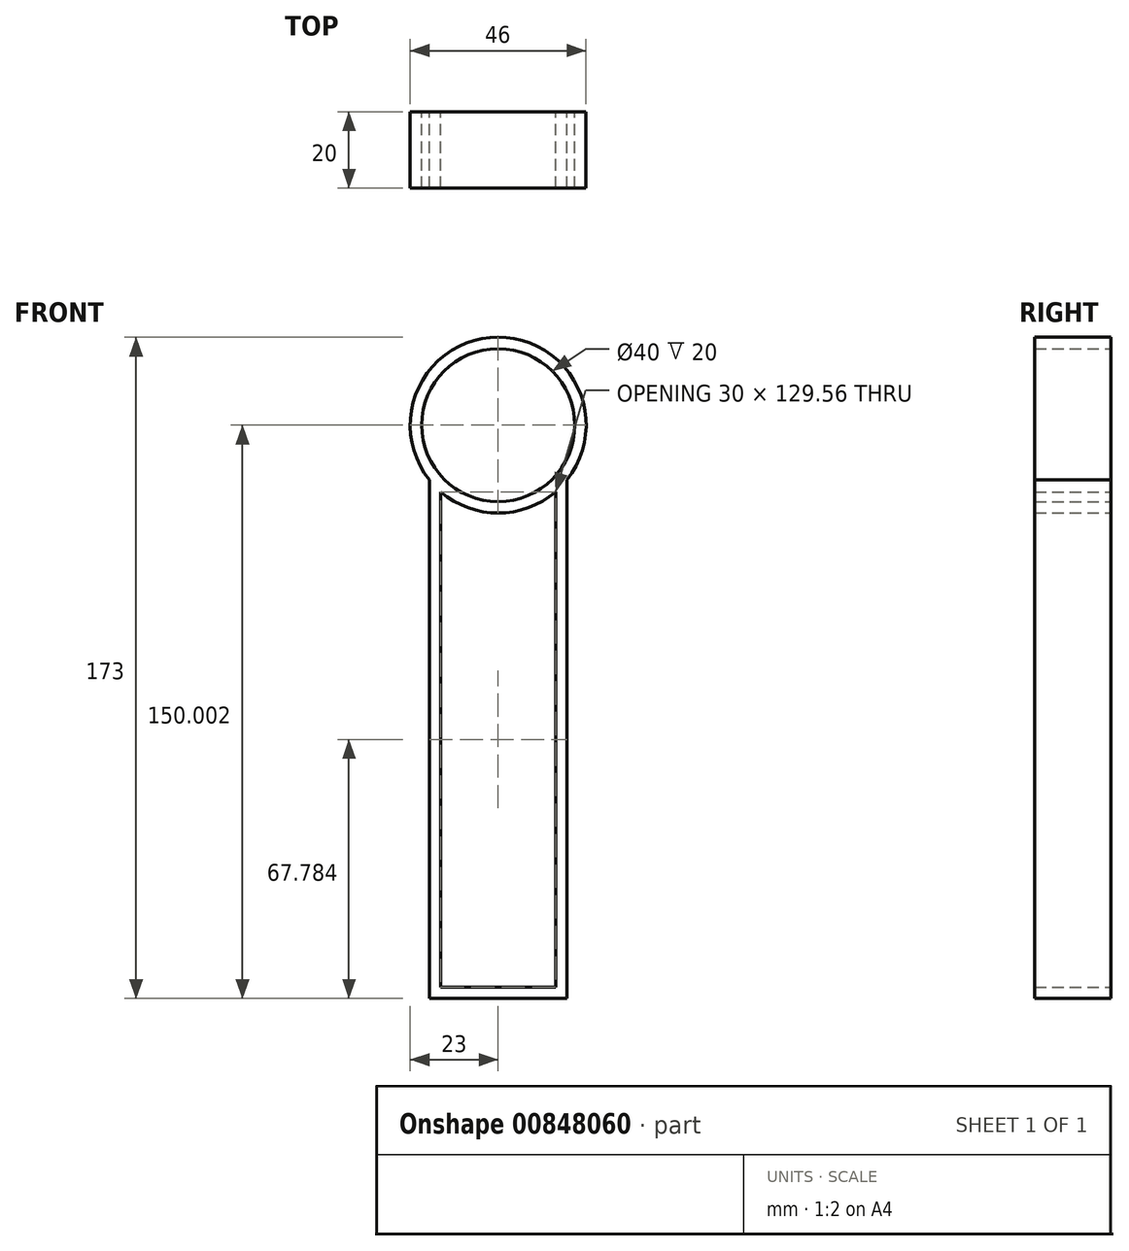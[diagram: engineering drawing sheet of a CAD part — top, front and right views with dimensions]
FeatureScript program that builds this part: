
annotation { "Feature Type Name" : "Feature", "Feature Type Description" : "" }
export const myFeature = defineFeature(function(context is Context, id is Id, definition is map)
    precondition{}
    {
        {
            var Q0;
            Q0=qCreatedBy(makeId("Front.planeOp"),FACE);
            var sketch = newSketch(context, id + "F0", { "sketchPlane" : qUnion([Q0])});
            skCircle(sketch, "E0", {"center": v(0, 77.07) * mm, "radius": 20 * mm});
            skCircle(sketch, "E1", {"center": v(0, 77.07) * mm, "radius": 23 * mm});
            skPoint(sketch, "E2.middle", {"position": v(0, 0) * mm});
            skLineSegment(sketch, "E3.bottom", {"start": v(-15, 69.93) * mm, "end": v(15, 69.93) * mm});
            skLineSegment(sketch, "E3.top", {"start": v(-15, -69.93) * mm, "end": v(15, -69.93) * mm});
            skLineSegment(sketch, "E3.left", {"start": v(-15, 69.93) * mm, "end": v(-15, -69.93) * mm});
            skLineSegment(sketch, "E3.right", {"start": v(15, 69.93) * mm, "end": v(15, -69.93) * mm});
            skLineSegment(sketch, "E4.bottom", {"start": v(-18, 72.93) * mm, "end": v(18, 72.93) * mm});
            skLineSegment(sketch, "E4.top", {"start": v(-18, -72.93) * mm, "end": v(18, -72.93) * mm});
            skLineSegment(sketch, "E4.left", {"start": v(-18, 72.93) * mm, "end": v(-18, -72.93) * mm});
            skLineSegment(sketch, "E4.right", {"start": v(18, 72.93) * mm, "end": v(18, -72.93) * mm});
            skSolve(sketch);
        }
        {
            var Q0;
            Q0=makeQuery(id+"F0.imprint","IMPRINT",FACE,{"disambiguationData":[TD([[makeQuery(id+"F0.imprint","IMPRINT",EDGE,{"derivedFrom":sQuery(id+"F0.wireOp",EDGE,"E0")}),-1.0]])]});
            var Q1;
            {var subQ0=sQuery(id+"F0.wireOp",EDGE,"W4g1jJkP-zB7D-7hkY-9fEf-dFhZXpONL2yB.left");var subQ1=sQuery(id+"F0.wireOp",EDGE,"E1");var subQ2=makeQuery(id+"F0.imprint","INTERSECT",VERTEX,{"derivedFrom":[subQ1,subQ0]});Q1=makeQuery(id+"F0.imprint","IMPRINT",FACE,{"disambiguationData":[TD([[makeQuery(id+"F0.imprint","IMPRINT",EDGE,{"disambiguationData":[TD([[subQ2,-1.0]])],"derivedFrom":subQ1}),-1.0]])]});}
            var Q2;
            {var subQ0=sQuery(id+"F0.wireOp",EDGE,"W4g1jJkP-zB7D-7hkY-9fEf-dFhZXpONL2yB.right");var subQ1=sQuery(id+"F0.wireOp",EDGE,"E1");var subQ2=makeQuery(id+"F0.imprint","INTERSECT",VERTEX,{"derivedFrom":[subQ1,subQ0]});Q2=makeQuery(id+"F0.imprint","IMPRINT",FACE,{"disambiguationData":[TD([[makeQuery(id+"F0.imprint","IMPRINT",EDGE,{"disambiguationData":[TD([[subQ2,1.0]])],"derivedFrom":subQ1}),-1.0]])]});}
            extrude(context, id + "F1", {"entities" : qUnion([Q0, Q1, Q2]), "depth" : 20 * mm, "offsetDistance" : 25 * mm});
        }
    });
